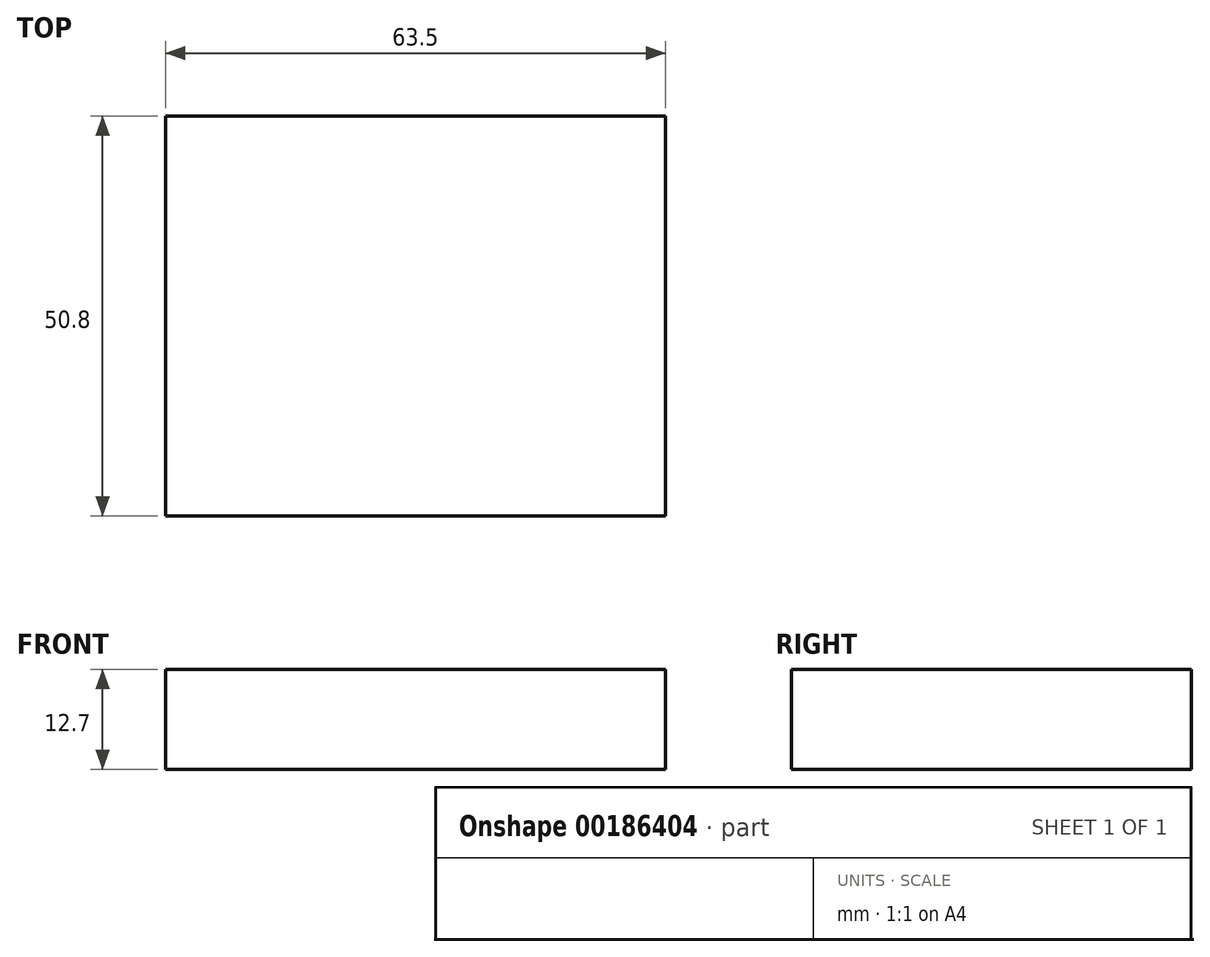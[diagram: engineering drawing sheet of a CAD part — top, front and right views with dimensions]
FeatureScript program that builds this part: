
annotation { "Feature Type Name" : "Feature", "Feature Type Description" : "" }
export const myFeature = defineFeature(function(context is Context, id is Id, definition is map)
    precondition{}
    {
        {
            var Q0;
            Q0=qCreatedBy(makeId("Top.planeOp"),FACE);
            var sketch = newSketch(context, id + "F0", { "sketchPlane" : qUnion([Q0])});
            skLineSegment(sketch, "E0.bottom", {"start": v(-35.02, 2.85) * mm, "end": v(28.48, 2.85) * mm});
            skLineSegment(sketch, "E0.top", {"start": v(-35.02, -47.95) * mm, "end": v(28.48, -47.95) * mm});
            skLineSegment(sketch, "E0.left", {"start": v(-35.02, 2.85) * mm, "end": v(-35.02, -47.95) * mm});
            skLineSegment(sketch, "E0.right", {"start": v(28.48, 2.85) * mm, "end": v(28.48, -47.95) * mm});
            skSolve(sketch);
        }
        {
            var Q0;
            Q0=makeQuery(id+"F0.imprint","IMPRINT",FACE,{"disambiguationData":[TD([[makeQuery(id+"F0.imprint","IMPRINT",EDGE,{"derivedFrom":sQuery(id+"F0.wireOp",EDGE,"E0.bottom")}),-1.0]])]});
            extrude(context, id + "F1", {"entities" : qUnion([Q0]), "depth" : 12.7 * mm});
        }
    });
